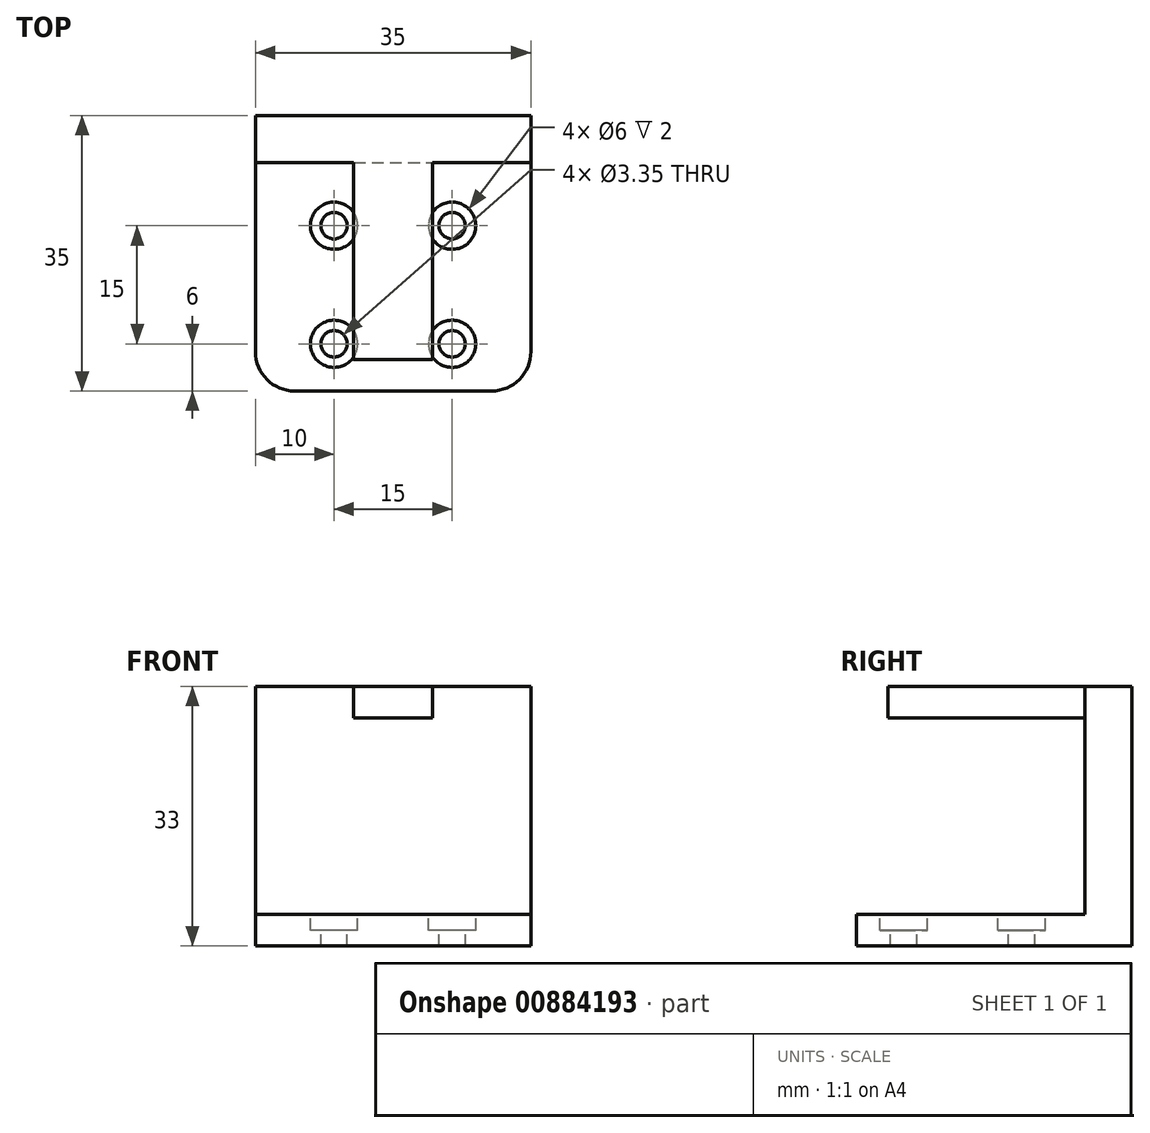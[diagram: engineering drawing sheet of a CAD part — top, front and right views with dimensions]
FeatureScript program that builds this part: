
annotation { "Feature Type Name" : "Feature", "Feature Type Description" : "" }
export const myFeature = defineFeature(function(context is Context, id is Id, definition is map)
    precondition{}
    {
        {
            var Q0;
            Q0=qCreatedBy(makeId("Top.planeOp"),FACE);
            var sketch = newSketch(context, id + "F0", { "sketchPlane" : qUnion([Q0])});
            skLineSegment(sketch, "E0.bottom", {"start": v(0, 0) * mm, "end": v(35, 0) * mm});
            skLineSegment(sketch, "E0.top", {"start": v(0, 35) * mm, "end": v(35, 35) * mm});
            skLineSegment(sketch, "E0.left", {"start": v(0, 0) * mm, "end": v(0, 35) * mm});
            skLineSegment(sketch, "E0.right", {"start": v(35, 0) * mm, "end": v(35, 35) * mm});
            skSolve(sketch);
        }
        {
            var Q0;
            Q0=qSketchRegion(id+"F0",true);
            extrude(context, id + "F1", {"entities" : qUnion([Q0]), "depth" : 4 * mm});
        }
        {
            var Q0;
            Q0=makeQuery(id+"F1.opExtrude","CAP_FACE",FACE,{"disambiguationData":[OSD([sQuery(id+"F0.wireOp",EDGE,"E0.bottom"),sQuery(id+"F0.wireOp",EDGE,"E0.top"),sQuery(id+"F0.wireOp",EDGE,"E0.left"),sQuery(id+"F0.wireOp",EDGE,"E0.right")])],"isStart":false});
            var sketch = newSketch(context, id + "F2", { "sketchPlane" : qUnion([Q0])});
            skCircle(sketch, "E1", {"center": v(10, 21) * mm, "radius": 1.68 * mm});
            skCircle(sketch, "E2", {"center": v(25, 21) * mm, "radius": 1.68 * mm});
            skCircle(sketch, "E3", {"center": v(10, 6) * mm, "radius": 1.68 * mm});
            skCircle(sketch, "E4", {"center": v(25, 6) * mm, "radius": 1.68 * mm});
            skLineSegment(sketch, "E5", {"start": v(10, 21) * mm, "end": v(0, 21) * mm});
            skLineSegment(sketch, "E6", {"start": v(25, 6) * mm, "end": v(35, 6) * mm});
            skCircle(sketch, "E7", {"center": v(10, 21) * mm, "radius": 3 * mm});
            skCircle(sketch, "E8", {"center": v(25, 21) * mm, "radius": 3 * mm});
            skCircle(sketch, "E9", {"center": v(10, 6) * mm, "radius": 3 * mm});
            skCircle(sketch, "E10", {"center": v(25, 6) * mm, "radius": 3 * mm});
            skLineSegment(sketch, "E11", {"start": v(10, 6) * mm, "end": v(10, 0) * mm});
            skSolve(sketch);
        }
        {
            var Q0;
            Q0=makeQuery(id+"F1.opExtrude","CAP_FACE",FACE,{"disambiguationData":[OSD([sQuery(id+"F0.wireOp",EDGE,"E0.bottom"),sQuery(id+"F0.wireOp",EDGE,"E0.top"),sQuery(id+"F0.wireOp",EDGE,"E0.left"),sQuery(id+"F0.wireOp",EDGE,"E0.right")])],"isStart":false});
            var sketch = newSketch(context, id + "F3", { "sketchPlane" : qUnion([Q0])});
            skLineSegment(sketch, "E12.bottom", {"start": v(0, 35) * mm, "end": v(35, 35) * mm});
            skLineSegment(sketch, "E12.top", {"start": v(0, 29) * mm, "end": v(35, 29) * mm});
            skLineSegment(sketch, "E12.left", {"start": v(0, 35) * mm, "end": v(0, 29) * mm});
            skLineSegment(sketch, "E12.right", {"start": v(35, 35) * mm, "end": v(35, 29) * mm});
            skSolve(sketch);
        }
        {
            var Q0;
            Q0=makeQuery(id+"F2.imprint","IMPRINT",FACE,{"disambiguationData":[TD([[makeQuery(id+"F2.imprint","IMPRINT",EDGE,{"derivedFrom":sQuery(id+"F2.wireOp",EDGE,"E1")}),-1.0]])]});
            var Q1;
            Q1=makeQuery(id+"F2.imprint","IMPRINT",FACE,{"disambiguationData":[TD([[makeQuery(id+"F2.imprint","IMPRINT",EDGE,{"derivedFrom":sQuery(id+"F2.wireOp",EDGE,"E2")}),-1.0]])]});
            var Q2;
            Q2=makeQuery(id+"F2.imprint","IMPRINT",FACE,{"disambiguationData":[TD([[makeQuery(id+"F2.imprint","IMPRINT",EDGE,{"derivedFrom":sQuery(id+"F2.wireOp",EDGE,"E4")}),-1.0]])]});
            var Q3;
            Q3=makeQuery(id+"F2.imprint","IMPRINT",FACE,{"disambiguationData":[TD([[makeQuery(id+"F2.imprint","IMPRINT",EDGE,{"derivedFrom":sQuery(id+"F2.wireOp",EDGE,"E3")}),-1.0]])]});
            extrude(context, id + "F4", {"entities" : qUnion([Q0, Q1, Q2, Q3]), "operationType" : NewBodyOperationType.REMOVE, "oppositeDirection" : true, "depth" : 2 * mm});
        }
        {
            var Q0;
            Q0=makeQuery(id+"F1.opExtrude","SWEPT_EDGE",EDGE,{"disambiguationData":[OSD([sQuery(id+"F0.wireOp",EDGE,"E0.bottom"),sQuery(id+"F0.wireOp",EDGE,"E0.left")])]});
            var Q1;
            Q1=makeQuery(id+"F1.opExtrude","SWEPT_EDGE",EDGE,{"disambiguationData":[OSD([sQuery(id+"F0.wireOp",EDGE,"E0.bottom"),sQuery(id+"F0.wireOp",EDGE,"E0.right")])]});
            fillet(context, id + "F5", {"entities" : qUnion([Q0, Q1]), "radius" : 5 * mm, "tangentPropagation" : true, "allowEdgeOverflow" : false});
        }
        {
            var Q0;
            Q0=makeQuery(id+"F2.imprint","IMPRINT",FACE,{"disambiguationData":[TD([[makeQuery(id+"F2.imprint","IMPRINT",EDGE,{"derivedFrom":sQuery(id+"F2.wireOp",EDGE,"E1")}),1.0]])]});
            var Q1;
            Q1=makeQuery(id+"F2.imprint","IMPRINT",FACE,{"disambiguationData":[TD([[makeQuery(id+"F2.imprint","IMPRINT",EDGE,{"derivedFrom":sQuery(id+"F2.wireOp",EDGE,"E2")}),1.0]])]});
            var Q2;
            Q2=makeQuery(id+"F2.imprint","IMPRINT",FACE,{"disambiguationData":[TD([[makeQuery(id+"F2.imprint","IMPRINT",EDGE,{"derivedFrom":sQuery(id+"F2.wireOp",EDGE,"E4")}),1.0]])]});
            var Q3;
            Q3=makeQuery(id+"F2.imprint","IMPRINT",FACE,{"disambiguationData":[TD([[makeQuery(id+"F2.imprint","IMPRINT",EDGE,{"derivedFrom":sQuery(id+"F2.wireOp",EDGE,"E3")}),1.0]])]});
            extrude(context, id + "F6", {"entities" : qUnion([Q0, Q1, Q2, Q3]), "operationType" : NewBodyOperationType.REMOVE, "oppositeDirection" : true, "depth" : 25 * mm, "symmetric" : true});
        }
        {
            var Q0;
            Q0=makeQuery(id+"F3.imprint","IMPRINT",FACE,{"disambiguationData":[TD([[makeQuery(id+"F3.imprint","IMPRINT",EDGE,{"derivedFrom":sQuery(id+"F3.wireOp",EDGE,"E12.bottom")}),-1.0]])]});
            extrude(context, id + "F7", {"entities" : qUnion([Q0]), "operationType" : NewBodyOperationType.ADD, "offsetDistance" : 25 * mm, "depth" : 29 * mm});
        }
        {
            var Q0;
            Q0=makeQuery(id+"F7.opExtrude","SWEPT_FACE",FACE,{"disambiguationData":[OSD([sQuery(id+"F3.wireOp",EDGE,"E12.top")])]});
            var sketch = newSketch(context, id + "F8", { "sketchPlane" : qUnion([Q0])});
            skLineSegment(sketch, "E13", {"start": v(17.5, 33) * mm, "end": v(12.5, 33) * mm});
            skLineSegment(sketch, "E14", {"start": v(12.5, 33) * mm, "end": v(12.5, 29) * mm});
            skLineSegment(sketch, "E15", {"start": v(12.5, 29) * mm, "end": v(22.5, 29) * mm});
            skLineSegment(sketch, "E16", {"start": v(22.5, 29) * mm, "end": v(22.5, 33) * mm});
            skLineSegment(sketch, "E17", {"start": v(17.5, 33) * mm, "end": v(22.5, 33) * mm});
            skSolve(sketch);
        }
        {
            var Q0;
            Q0=makeQuery(id+"F8.imprint","IMPRINT",FACE,{"disambiguationData":[TD([[makeQuery(id+"F8.imprint","IMPRINT",EDGE,{"derivedFrom":sQuery(id+"F8.wireOp",EDGE,"E13")}),-1.0]])]});
            extrude(context, id + "F9", {"entities" : qUnion([Q0]), "operationType" : NewBodyOperationType.ADD, "depth" : 25 * mm, "offsetDistance" : 25 * mm});
        }
    });
